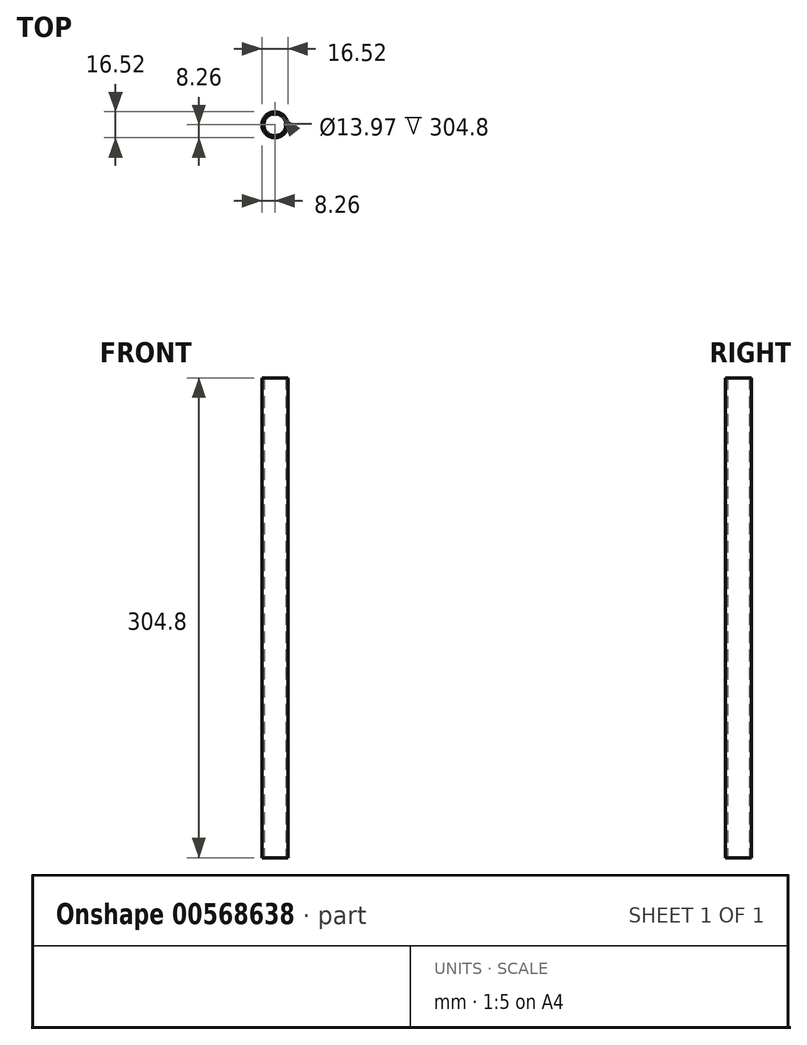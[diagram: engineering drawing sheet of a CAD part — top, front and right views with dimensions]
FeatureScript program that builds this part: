
annotation { "Feature Type Name" : "Feature", "Feature Type Description" : "" }
export const myFeature = defineFeature(function(context is Context, id is Id, definition is map)
    precondition{}
    {
        {
            var Q0;
            Q0=qCreatedBy(makeId("Top.planeOp"),FACE);
            var sketch = newSketch(context, id + "F0", { "sketchPlane" : qUnion([Q0])});
            skCircle(sketch, "E0", {"center": v(0, 0) * mm, "radius": 8.26 * mm});
            skCircle(sketch, "E1", {"center": v(0, 0) * mm, "radius": 6.99 * mm});
            skSolve(sketch);
        }
        {
            var Q0;
            Q0 = qSketchRegion(id + "F0", true);
            extrude(context, id + "F1", {"entities" : qUnion([Q0]), "depth" : 304.8 * mm, "offsetDistance" : 25.4 * mm});
        }
    });
